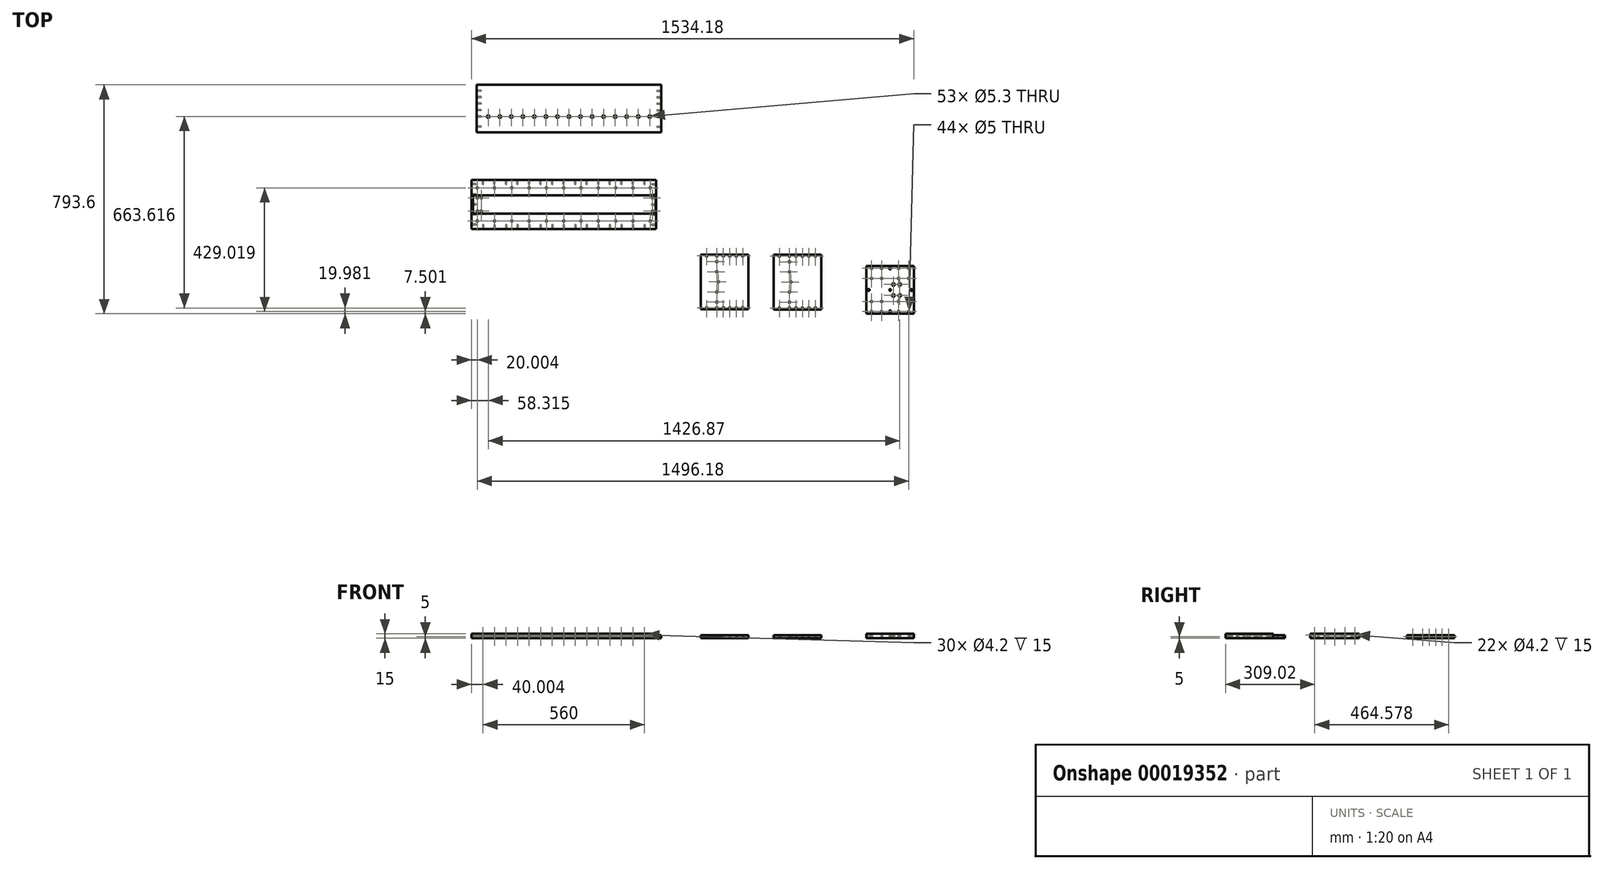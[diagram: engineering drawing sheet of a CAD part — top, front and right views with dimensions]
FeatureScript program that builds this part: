
annotation { "Feature Type Name" : "Feature", "Feature Type Description" : "" }
export const myFeature = defineFeature(function(context is Context, id is Id, definition is map)
    precondition{}
    {
        {
            var Q0;
            Q0=qCreatedBy(makeId("Top.planeOp"),FACE);
            var sketch = newSketch(context, id + "F0", { "sketchPlane" : qUnion([Q0])});
            skLineSegment(sketch, "E0.bottom", {"start": v(-320.38, 53) * mm, "end": v(319.62, 53) * mm});
            skLineSegment(sketch, "E0.top", {"start": v(-320.38, -117) * mm, "end": v(319.62, -117) * mm});
            skLineSegment(sketch, "E0.left", {"start": v(-320.38, 53) * mm, "end": v(-320.38, -117) * mm});
            skLineSegment(sketch, "E0.right", {"start": v(319.62, 53) * mm, "end": v(319.62, -117) * mm});
            skLineSegment(sketch, "E1.right", {"start": v(337.93, 382.58) * mm, "end": v(337.93, 217.58) * mm});
            skLineSegment(sketch, "E1.left", {"start": v(-302.07, 382.58) * mm, "end": v(-302.07, 217.58) * mm});
            skLineSegment(sketch, "E1.top", {"start": v(-302.07, 217.58) * mm, "end": v(337.93, 217.58) * mm});
            skLineSegment(sketch, "E1.bottom", {"start": v(-302.07, 382.58) * mm, "end": v(337.93, 382.58) * mm});
            skLineSegment(sketch, "E2.bottom", {"start": v(475.41, -205.5) * mm, "end": v(640.41, -205.5) * mm});
            skLineSegment(sketch, "E2.top", {"start": v(475.41, -395.5) * mm, "end": v(640.41, -395.5) * mm});
            skLineSegment(sketch, "E2.left", {"start": v(475.41, -205.5) * mm, "end": v(475.41, -395.5) * mm});
            skLineSegment(sketch, "E2.right", {"start": v(640.41, -205.5) * mm, "end": v(640.41, -395.5) * mm});
            skCircle(sketch, "E3", {"center": v(575.41, -210.5) * mm, "radius": 2.65 * mm});
            skCircle(sketch, "E4", {"center": v(620.41, -210.5) * mm, "radius": 2.65 * mm});
            skCircle(sketch, "E5", {"center": v(597.91, -210.5) * mm, "radius": 2.65 * mm});
            skCircle(sketch, "E6", {"center": v(552.91, -210.5) * mm, "radius": 2.65 * mm});
            skCircle(sketch, "E7", {"center": v(495.41, -210.5) * mm, "radius": 2.65 * mm});
            skCircle(sketch, "E8", {"center": v(530.41, -210.5) * mm, "radius": 2.65 * mm});
            skCircle(sketch, "E9", {"center": v(575.41, -390.5) * mm, "radius": 2.65 * mm});
            skCircle(sketch, "E10", {"center": v(552.91, -390.5) * mm, "radius": 2.65 * mm});
            skCircle(sketch, "E11", {"center": v(597.91, -390.5) * mm, "radius": 2.65 * mm});
            skCircle(sketch, "E12", {"center": v(620.41, -390.5) * mm, "radius": 2.65 * mm});
            skCircle(sketch, "E13", {"center": v(530.41, -390.5) * mm, "radius": 2.65 * mm});
            skCircle(sketch, "E14", {"center": v(495.41, -390.5) * mm, "radius": 2.65 * mm});
            skCircle(sketch, "E15", {"center": v(530.41, -230.5) * mm, "radius": 2.65 * mm});
            skCircle(sketch, "E16", {"center": v(530.41, -265.5) * mm, "radius": 2.65 * mm});
            skCircle(sketch, "E17", {"center": v(535.41, -300.5) * mm, "radius": 2.65 * mm});
            skCircle(sketch, "E18", {"center": v(530.41, -335.5) * mm, "radius": 2.65 * mm});
            skCircle(sketch, "E19", {"center": v(530.41, -370.5) * mm, "radius": 2.65 * mm});
            skLineSegment(sketch, "E20.top", {"start": v(727.45, -396.04) * mm, "end": v(892.45, -396.04) * mm});
            skLineSegment(sketch, "E20.bottom", {"start": v(727.45, -206.04) * mm, "end": v(892.45, -206.04) * mm});
            skLineSegment(sketch, "E20.right", {"start": v(892.45, -206.04) * mm, "end": v(892.45, -396.04) * mm});
            skLineSegment(sketch, "E20.left", {"start": v(727.45, -206.04) * mm, "end": v(727.45, -396.04) * mm});
            skCircle(sketch, "E21", {"center": v(849.95, -211.04) * mm, "radius": 2.65 * mm});
            skCircle(sketch, "E22", {"center": v(804.95, -391.04) * mm, "radius": 2.65 * mm});
            skCircle(sketch, "E23", {"center": v(787.45, -301.04) * mm, "radius": 2.65 * mm});
            skCircle(sketch, "E24", {"center": v(872.45, -211.04) * mm, "radius": 2.65 * mm});
            skCircle(sketch, "E25", {"center": v(782.45, -231.04) * mm, "radius": 2.65 * mm});
            skCircle(sketch, "E26", {"center": v(782.45, -266.04) * mm, "radius": 2.65 * mm});
            skCircle(sketch, "E27", {"center": v(849.95, -391.04) * mm, "radius": 2.65 * mm});
            skCircle(sketch, "E28", {"center": v(782.45, -211.04) * mm, "radius": 2.65 * mm});
            skCircle(sketch, "E29", {"center": v(872.45, -391.04) * mm, "radius": 2.65 * mm});
            skCircle(sketch, "E30", {"center": v(804.95, -211.04) * mm, "radius": 2.65 * mm});
            skCircle(sketch, "E31", {"center": v(782.45, -391.04) * mm, "radius": 2.65 * mm});
            skCircle(sketch, "E32", {"center": v(782.45, -336.04) * mm, "radius": 2.65 * mm});
            skCircle(sketch, "E33", {"center": v(747.45, -391.04) * mm, "radius": 2.65 * mm});
            skCircle(sketch, "E34", {"center": v(782.45, -371.04) * mm, "radius": 2.65 * mm});
            skCircle(sketch, "E35", {"center": v(747.45, -211.04) * mm, "radius": 2.65 * mm});
            skCircle(sketch, "E36", {"center": v(827.45, -391.04) * mm, "radius": 2.65 * mm});
            skCircle(sketch, "E37", {"center": v(827.45, -211.04) * mm, "radius": 2.65 * mm});
            skCircle(sketch, "E38", {"center": v(-300.38, -89.5) * mm, "radius": 2.5 * mm});
            skCircle(sketch, "E39", {"center": v(-240.38, -89.5) * mm, "radius": 2.5 * mm});
            skCircle(sketch, "E40", {"center": v(-180.38, -89.5) * mm, "radius": 2.5 * mm});
            skCircle(sketch, "E41", {"center": v(-120.38, -89.5) * mm, "radius": 2.5 * mm});
            skCircle(sketch, "E42", {"center": v(-60.38, -89.5) * mm, "radius": 2.5 * mm});
            skCircle(sketch, "E43", {"center": v(-0.38, -89.5) * mm, "radius": 2.5 * mm});
            skCircle(sketch, "E44", {"center": v(59.62, -89.5) * mm, "radius": 2.5 * mm});
            skCircle(sketch, "E45", {"center": v(119.62, -89.5) * mm, "radius": 2.5 * mm});
            skCircle(sketch, "E46", {"center": v(179.62, -89.5) * mm, "radius": 2.5 * mm});
            skCircle(sketch, "E47", {"center": v(239.62, -89.5) * mm, "radius": 2.5 * mm});
            skCircle(sketch, "E48", {"center": v(299.62, -89.5) * mm, "radius": 2.5 * mm});
            skCircle(sketch, "E49", {"center": v(-180.38, 25.5) * mm, "radius": 2.5 * mm});
            skCircle(sketch, "E50", {"center": v(-120.38, 25.5) * mm, "radius": 2.5 * mm});
            skCircle(sketch, "E51", {"center": v(119.62, 25.5) * mm, "radius": 2.5 * mm});
            skCircle(sketch, "E52", {"center": v(-60.38, 25.5) * mm, "radius": 2.5 * mm});
            skCircle(sketch, "E53", {"center": v(-0.38, 25.5) * mm, "radius": 2.5 * mm});
            skCircle(sketch, "E54", {"center": v(239.62, 25.5) * mm, "radius": 2.5 * mm});
            skCircle(sketch, "E55", {"center": v(-240.38, 25.5) * mm, "radius": 2.5 * mm});
            skCircle(sketch, "E56", {"center": v(299.62, 25.5) * mm, "radius": 2.5 * mm});
            skCircle(sketch, "E57", {"center": v(59.62, 25.5) * mm, "radius": 2.5 * mm});
            skCircle(sketch, "E58", {"center": v(179.62, 25.5) * mm, "radius": 2.5 * mm});
            skCircle(sketch, "E59", {"center": v(-300.38, 25.5) * mm, "radius": 2.5 * mm});
            skCircle(sketch, "E60", {"center": v(307.62, -9) * mm, "radius": 2.5 * mm});
            skCircle(sketch, "E61", {"center": v(307.62, -55) * mm, "radius": 2.5 * mm});
            skPoint(sketch, "E62", {"position": v(319.62, -32) * mm});
            skCircle(sketch, "E63", {"center": v(-299.38, -9) * mm, "radius": 2.5 * mm});
            skCircle(sketch, "E64", {"center": v(-299.38, -55) * mm, "radius": 2.5 * mm});
            skCircle(sketch, "E65", {"center": v(-286.38, -9) * mm, "radius": 2.5 * mm});
            skCircle(sketch, "E66", {"center": v(-286.38, -55) * mm, "radius": 2.5 * mm});
            skPoint(sketch, "E67", {"position": v(-320.38, -32) * mm});
            skLineSegment(sketch, "E68.bottom", {"start": v(1048.8, -246.02) * mm, "end": v(1213.8, -246.02) * mm});
            skLineSegment(sketch, "E68.top", {"start": v(1048.8, -411.02) * mm, "end": v(1213.8, -411.02) * mm});
            skLineSegment(sketch, "E68.left", {"start": v(1048.8, -246.02) * mm, "end": v(1048.8, -411.02) * mm});
            skLineSegment(sketch, "E68.right", {"start": v(1213.8, -246.02) * mm, "end": v(1213.8, -411.02) * mm});
            skCircle(sketch, "E69", {"center": v(1066.8, -253.52) * mm, "radius": 2.5 * mm});
            skCircle(sketch, "E70", {"center": v(1101.8, -253.52) * mm, "radius": 2.5 * mm});
            skCircle(sketch, "E71", {"center": v(1066.8, -288.52) * mm, "radius": 2.5 * mm});
            skCircle(sketch, "E72", {"center": v(1101.8, -288.52) * mm, "radius": 2.5 * mm});
            skCircle(sketch, "E73", {"center": v(1160.8, -253.52) * mm, "radius": 2.5 * mm});
            skCircle(sketch, "E74", {"center": v(1195.8, -288.52) * mm, "radius": 2.5 * mm});
            skCircle(sketch, "E75", {"center": v(1160.8, -288.52) * mm, "radius": 2.5 * mm});
            skCircle(sketch, "E76", {"center": v(1195.8, -253.52) * mm, "radius": 2.5 * mm});
            skCircle(sketch, "E77", {"center": v(1066.8, -368.52) * mm, "radius": 2.5 * mm});
            skCircle(sketch, "E78", {"center": v(1101.8, -403.52) * mm, "radius": 2.5 * mm});
            skCircle(sketch, "E79", {"center": v(1066.8, -403.52) * mm, "radius": 2.5 * mm});
            skCircle(sketch, "E80", {"center": v(1101.8, -368.52) * mm, "radius": 2.5 * mm});
            skCircle(sketch, "E81", {"center": v(1160.8, -368.52) * mm, "radius": 2.5 * mm});
            skCircle(sketch, "E82", {"center": v(1195.8, -403.52) * mm, "radius": 2.5 * mm});
            skCircle(sketch, "E83", {"center": v(1160.8, -403.52) * mm, "radius": 2.5 * mm});
            skCircle(sketch, "E84", {"center": v(1195.8, -368.52) * mm, "radius": 2.5 * mm});
            skPoint(sketch, "E85", {"position": v(1048.8, -328.52) * mm});
            skPoint(sketch, "E86", {"position": v(1131.3, -411.02) * mm});
            skCircle(sketch, "E87", {"center": v(1056.8, -328.52) * mm, "radius": 3.35 * mm});
            skCircle(sketch, "E88", {"center": v(1205.8, -328.52) * mm, "radius": 3.35 * mm});
            skCircle(sketch, "E89", {"center": v(1131.3, -403.02) * mm, "radius": 3.35 * mm});
            skCircle(sketch, "E90", {"center": v(1131.3, -254.02) * mm, "radius": 3.35 * mm});
            skCircle(sketch, "E91", {"center": v(1131.3, -328.52) * mm, "radius": 3 * mm});
            skCircle(sketch, "E92", {"center": v(1142.8, -309.52) * mm, "radius": 2.65 * mm});
            skCircle(sketch, "E93", {"center": v(1164.8, -309.52) * mm, "radius": 2.65 * mm});
            skCircle(sketch, "E94", {"center": v(1142.8, -347.52) * mm, "radius": 2.65 * mm});
            skCircle(sketch, "E95", {"center": v(1164.8, -347.52) * mm, "radius": 2.65 * mm});
            skCircle(sketch, "E96", {"center": v(1142.8, -309.52) * mm, "radius": 4.75 * mm});
            skCircle(sketch, "E97", {"center": v(1164.8, -309.52) * mm, "radius": 4.75 * mm});
            skCircle(sketch, "E98", {"center": v(1142.8, -347.52) * mm, "radius": 4.75 * mm});
            skCircle(sketch, "E99", {"center": v(1164.8, -347.52) * mm, "radius": 4.75 * mm});
            skSolve(sketch);
        }
        {
            var Q0;
            Q0=makeQuery(id+"F0.imprint","IMPRINT",FACE,{"disambiguationData":[TD([[makeQuery(id+"F0.imprint","IMPRINT",EDGE,{"derivedFrom":sQuery(id+"F0.wireOp",EDGE,"E0.bottom")}),-1.0]])]});
            var Q1;
            Q1=makeQuery(id+"F0.imprint","IMPRINT",FACE,{"disambiguationData":[TD([[makeQuery(id+"F0.imprint","IMPRINT",EDGE,{"derivedFrom":sQuery(id+"F0.wireOp",EDGE,"E60")}),-1.0]])]});
            extrude(context, id + "F1", {"entities" : qUnion([Q0, Q1]), "depth" : 15 * mm});
        }
        {
            var Q0;
            Q0=makeQuery(id+"F0.imprint","IMPRINT",FACE,{"disambiguationData":[TD([[makeQuery(id+"F0.imprint","IMPRINT",EDGE,{"derivedFrom":sQuery(id+"F0.wireOp",EDGE,"E1.right")}),-1.0]])]});
            extrude(context, id + "F2", {"entities" : qUnion([Q0]), "depth" : 10 * mm});
        }
        {
            var Q0;
            Q0=makeQuery(id+"F1.opExtrude","SWEPT_FACE",FACE,{"disambiguationData":[OSD([sQuery(id+"F0.wireOp",EDGE,"E0.top")])]});
            var sketch = newSketch(context, id + "F3", { "sketchPlane" : qUnion([Q0])});
            skCircle(sketch, "E100", {"center": v(-0.38, 10) * mm, "radius": 2.1 * mm});
            skCircle(sketch, "E101", {"center": v(39.62, 10) * mm, "radius": 2.1 * mm});
            skCircle(sketch, "E102", {"center": v(79.62, 10) * mm, "radius": 2.1 * mm});
            skCircle(sketch, "E103", {"center": v(119.62, 10) * mm, "radius": 2.1 * mm});
            skCircle(sketch, "E104", {"center": v(159.62, 10) * mm, "radius": 2.1 * mm});
            skCircle(sketch, "E105", {"center": v(199.62, 10) * mm, "radius": 2.1 * mm});
            skCircle(sketch, "E106", {"center": v(239.62, 10) * mm, "radius": 2.1 * mm});
            skCircle(sketch, "E107", {"center": v(-40.38, 10) * mm, "radius": 2.1 * mm});
            skCircle(sketch, "E108", {"center": v(-80.38, 10) * mm, "radius": 2.1 * mm});
            skCircle(sketch, "E109", {"center": v(-120.38, 10) * mm, "radius": 2.1 * mm});
            skCircle(sketch, "E110", {"center": v(-160.38, 10) * mm, "radius": 2.1 * mm});
            skCircle(sketch, "E111", {"center": v(-200.38, 10) * mm, "radius": 2.1 * mm});
            skCircle(sketch, "E112", {"center": v(-240.38, 10) * mm, "radius": 2.1 * mm});
            skCircle(sketch, "E113", {"center": v(279.62, 10) * mm, "radius": 2.1 * mm});
            skCircle(sketch, "E114", {"center": v(-280.38, 10) * mm, "radius": 2.1 * mm});
            skSolve(sketch);
        }
        {
            var Q0;
            Q0=makeQuery(id+"F1.opExtrude","SWEPT_FACE",FACE,{"disambiguationData":[OSD([sQuery(id+"F0.wireOp",EDGE,"E0.bottom")])]});
            var sketch = newSketch(context, id + "F4", { "sketchPlane" : qUnion([Q0])});
            skCircle(sketch, "E115", {"center": v(120.38, 5) * mm, "radius": 2.1 * mm});
            skCircle(sketch, "E116", {"center": v(280.38, 5) * mm, "radius": 2.1 * mm});
            skCircle(sketch, "E117", {"center": v(0.38, 5) * mm, "radius": 2.1 * mm});
            skCircle(sketch, "E118", {"center": v(-239.62, 5) * mm, "radius": 2.1 * mm});
            skCircle(sketch, "E119", {"center": v(-199.62, 5) * mm, "radius": 2.1 * mm});
            skCircle(sketch, "E120", {"center": v(-159.62, 5) * mm, "radius": 2.1 * mm});
            skCircle(sketch, "E121", {"center": v(-119.62, 5) * mm, "radius": 2.1 * mm});
            skCircle(sketch, "E122", {"center": v(-79.62, 5) * mm, "radius": 2.1 * mm});
            skCircle(sketch, "E123", {"center": v(-39.62, 5) * mm, "radius": 2.1 * mm});
            skCircle(sketch, "E124", {"center": v(80.38, 5) * mm, "radius": 2.1 * mm});
            skCircle(sketch, "E125", {"center": v(240.38, 5) * mm, "radius": 2.1 * mm});
            skCircle(sketch, "E126", {"center": v(-279.62, 5) * mm, "radius": 2.1 * mm});
            skCircle(sketch, "E127", {"center": v(200.38, 5) * mm, "radius": 2.1 * mm});
            skCircle(sketch, "E128", {"center": v(160.38, 5) * mm, "radius": 2.1 * mm});
            skCircle(sketch, "E129", {"center": v(40.38, 5) * mm, "radius": 2.1 * mm});
            skSolve(sketch);
        }
        {
            var Q0;
            Q0=makeQuery(id+"F4.imprint","IMPRINT",FACE,{"disambiguationData":[TD([[makeQuery(id+"F4.imprint","IMPRINT",EDGE,{"derivedFrom":sQuery(id+"F4.wireOp",EDGE,"E116")}),1.0]])]});
            var Q1;
            Q1=makeQuery(id+"F4.imprint","IMPRINT",FACE,{"disambiguationData":[TD([[makeQuery(id+"F4.imprint","IMPRINT",EDGE,{"derivedFrom":sQuery(id+"F4.wireOp",EDGE,"E125")}),1.0]])]});
            var Q2;
            Q2=makeQuery(id+"F4.imprint","IMPRINT",FACE,{"disambiguationData":[TD([[makeQuery(id+"F4.imprint","IMPRINT",EDGE,{"derivedFrom":sQuery(id+"F4.wireOp",EDGE,"E127")}),1.0]])]});
            var Q3;
            Q3=makeQuery(id+"F4.imprint","IMPRINT",FACE,{"disambiguationData":[TD([[makeQuery(id+"F4.imprint","IMPRINT",EDGE,{"derivedFrom":sQuery(id+"F4.wireOp",EDGE,"E128")}),1.0]])]});
            var Q4;
            Q4=makeQuery(id+"F4.imprint","IMPRINT",FACE,{"disambiguationData":[TD([[makeQuery(id+"F4.imprint","IMPRINT",EDGE,{"derivedFrom":sQuery(id+"F4.wireOp",EDGE,"E115")}),1.0]])]});
            var Q5;
            Q5=makeQuery(id+"F4.imprint","IMPRINT",FACE,{"disambiguationData":[TD([[makeQuery(id+"F4.imprint","IMPRINT",EDGE,{"derivedFrom":sQuery(id+"F4.wireOp",EDGE,"E124")}),1.0]])]});
            var Q6;
            Q6=makeQuery(id+"F4.imprint","IMPRINT",FACE,{"disambiguationData":[TD([[makeQuery(id+"F4.imprint","IMPRINT",EDGE,{"derivedFrom":sQuery(id+"F4.wireOp",EDGE,"E129")}),1.0]])]});
            var Q7;
            Q7=makeQuery(id+"F4.imprint","IMPRINT",FACE,{"disambiguationData":[TD([[makeQuery(id+"F4.imprint","IMPRINT",EDGE,{"derivedFrom":sQuery(id+"F4.wireOp",EDGE,"E117")}),1.0]])]});
            var Q8;
            Q8=makeQuery(id+"F4.imprint","IMPRINT",FACE,{"disambiguationData":[TD([[makeQuery(id+"F4.imprint","IMPRINT",EDGE,{"derivedFrom":sQuery(id+"F4.wireOp",EDGE,"E123")}),1.0]])]});
            var Q9;
            Q9=makeQuery(id+"F4.imprint","IMPRINT",FACE,{"disambiguationData":[TD([[makeQuery(id+"F4.imprint","IMPRINT",EDGE,{"derivedFrom":sQuery(id+"F4.wireOp",EDGE,"E122")}),1.0]])]});
            var Q10;
            Q10=makeQuery(id+"F4.imprint","IMPRINT",FACE,{"disambiguationData":[TD([[makeQuery(id+"F4.imprint","IMPRINT",EDGE,{"derivedFrom":sQuery(id+"F4.wireOp",EDGE,"E121")}),1.0]])]});
            var Q11;
            Q11=makeQuery(id+"F4.imprint","IMPRINT",FACE,{"disambiguationData":[TD([[makeQuery(id+"F4.imprint","IMPRINT",EDGE,{"derivedFrom":sQuery(id+"F4.wireOp",EDGE,"E120")}),1.0]])]});
            var Q12;
            Q12=makeQuery(id+"F4.imprint","IMPRINT",FACE,{"disambiguationData":[TD([[makeQuery(id+"F4.imprint","IMPRINT",EDGE,{"derivedFrom":sQuery(id+"F4.wireOp",EDGE,"E119")}),1.0]])]});
            var Q13;
            Q13=makeQuery(id+"F4.imprint","IMPRINT",FACE,{"disambiguationData":[TD([[makeQuery(id+"F4.imprint","IMPRINT",EDGE,{"derivedFrom":sQuery(id+"F4.wireOp",EDGE,"E118")}),1.0]])]});
            var Q14;
            Q14=makeQuery(id+"F4.imprint","IMPRINT",FACE,{"disambiguationData":[TD([[makeQuery(id+"F4.imprint","IMPRINT",EDGE,{"derivedFrom":sQuery(id+"F4.wireOp",EDGE,"E126")}),1.0]])]});
            extrude(context, id + "F5", {"entities" : qUnion([Q0, Q1, Q2, Q3, Q4, Q5, Q6, Q7, Q8, Q9, Q10, Q11, Q12, Q13, Q14]), "operationType" : NewBodyOperationType.REMOVE, "oppositeDirection" : true, "depth" : 15 * mm});
        }
        {
            var Q0;
            Q0=makeQuery(id+"F3.imprint","IMPRINT",FACE,{"disambiguationData":[TD([[makeQuery(id+"F3.imprint","IMPRINT",EDGE,{"derivedFrom":sQuery(id+"F3.wireOp",EDGE,"E113")}),1.0]])]});
            var Q1;
            Q1=makeQuery(id+"F3.imprint","IMPRINT",FACE,{"disambiguationData":[TD([[makeQuery(id+"F3.imprint","IMPRINT",EDGE,{"derivedFrom":sQuery(id+"F3.wireOp",EDGE,"E106")}),1.0]])]});
            var Q2;
            Q2=makeQuery(id+"F3.imprint","IMPRINT",FACE,{"disambiguationData":[TD([[makeQuery(id+"F3.imprint","IMPRINT",EDGE,{"derivedFrom":sQuery(id+"F3.wireOp",EDGE,"E105")}),1.0]])]});
            var Q3;
            Q3=makeQuery(id+"F3.imprint","IMPRINT",FACE,{"disambiguationData":[TD([[makeQuery(id+"F3.imprint","IMPRINT",EDGE,{"derivedFrom":sQuery(id+"F3.wireOp",EDGE,"E104")}),1.0]])]});
            var Q4;
            Q4=makeQuery(id+"F3.imprint","IMPRINT",FACE,{"disambiguationData":[TD([[makeQuery(id+"F3.imprint","IMPRINT",EDGE,{"derivedFrom":sQuery(id+"F3.wireOp",EDGE,"E103")}),1.0]])]});
            var Q5;
            Q5=makeQuery(id+"F3.imprint","IMPRINT",FACE,{"disambiguationData":[TD([[makeQuery(id+"F3.imprint","IMPRINT",EDGE,{"derivedFrom":sQuery(id+"F3.wireOp",EDGE,"E102")}),1.0]])]});
            var Q6;
            Q6=makeQuery(id+"F3.imprint","IMPRINT",FACE,{"disambiguationData":[TD([[makeQuery(id+"F3.imprint","IMPRINT",EDGE,{"derivedFrom":sQuery(id+"F3.wireOp",EDGE,"E101")}),1.0]])]});
            var Q7;
            Q7=makeQuery(id+"F3.imprint","IMPRINT",FACE,{"disambiguationData":[TD([[makeQuery(id+"F3.imprint","IMPRINT",EDGE,{"derivedFrom":sQuery(id+"F3.wireOp",EDGE,"E100")}),1.0]])]});
            var Q8;
            Q8=makeQuery(id+"F3.imprint","IMPRINT",FACE,{"disambiguationData":[TD([[makeQuery(id+"F3.imprint","IMPRINT",EDGE,{"derivedFrom":sQuery(id+"F3.wireOp",EDGE,"E107")}),1.0]])]});
            var Q9;
            Q9=makeQuery(id+"F3.imprint","IMPRINT",FACE,{"disambiguationData":[TD([[makeQuery(id+"F3.imprint","IMPRINT",EDGE,{"derivedFrom":sQuery(id+"F3.wireOp",EDGE,"E108")}),1.0]])]});
            var Q10;
            Q10=makeQuery(id+"F3.imprint","IMPRINT",FACE,{"disambiguationData":[TD([[makeQuery(id+"F3.imprint","IMPRINT",EDGE,{"derivedFrom":sQuery(id+"F3.wireOp",EDGE,"E109")}),1.0]])]});
            var Q11;
            Q11=makeQuery(id+"F3.imprint","IMPRINT",FACE,{"disambiguationData":[TD([[makeQuery(id+"F3.imprint","IMPRINT",EDGE,{"derivedFrom":sQuery(id+"F3.wireOp",EDGE,"E110")}),1.0]])]});
            var Q12;
            Q12=makeQuery(id+"F3.imprint","IMPRINT",FACE,{"disambiguationData":[TD([[makeQuery(id+"F3.imprint","IMPRINT",EDGE,{"derivedFrom":sQuery(id+"F3.wireOp",EDGE,"E111")}),1.0]])]});
            var Q13;
            Q13=makeQuery(id+"F3.imprint","IMPRINT",FACE,{"disambiguationData":[TD([[makeQuery(id+"F3.imprint","IMPRINT",EDGE,{"derivedFrom":sQuery(id+"F3.wireOp",EDGE,"E112")}),1.0]])]});
            var Q14;
            Q14=makeQuery(id+"F3.imprint","IMPRINT",FACE,{"disambiguationData":[TD([[makeQuery(id+"F3.imprint","IMPRINT",EDGE,{"derivedFrom":sQuery(id+"F3.wireOp",EDGE,"E114")}),1.0]])]});
            extrude(context, id + "F6", {"entities" : qUnion([Q0, Q1, Q2, Q3, Q4, Q5, Q6, Q7, Q8, Q9, Q10, Q11, Q12, Q13, Q14]), "operationType" : NewBodyOperationType.REMOVE, "oppositeDirection" : true, "depth" : 15 * mm});
        }
        {
            var Q0;
            Q0=makeQuery(id+"F1.opExtrude","SWEPT_FACE",FACE,{"disambiguationData":[OSD([sQuery(id+"F0.wireOp",EDGE,"E0.left")])]});
            var sketch = newSketch(context, id + "F7", { "sketchPlane" : qUnion([Q0])});
            skCircle(sketch, "E130", {"center": v(-38, 10) * mm, "radius": 2.1 * mm});
            skCircle(sketch, "E131", {"center": v(-3, 10) * mm, "radius": 2.1 * mm});
            skCircle(sketch, "E132", {"center": v(32, 5) * mm, "radius": 2.1 * mm});
            skCircle(sketch, "E133", {"center": v(67, 10) * mm, "radius": 2.1 * mm});
            skCircle(sketch, "E134", {"center": v(102, 10) * mm, "radius": 2.1 * mm});
            skSolve(sketch);
        }
        {
            var Q0;
            Q0=makeQuery(id+"F7.imprint","IMPRINT",FACE,{"disambiguationData":[TD([[makeQuery(id+"F7.imprint","IMPRINT",EDGE,{"derivedFrom":sQuery(id+"F7.wireOp",EDGE,"E130")}),1.0]])]});
            var Q1;
            Q1=makeQuery(id+"F7.imprint","IMPRINT",FACE,{"disambiguationData":[TD([[makeQuery(id+"F7.imprint","IMPRINT",EDGE,{"derivedFrom":sQuery(id+"F7.wireOp",EDGE,"E131")}),1.0]])]});
            var Q2;
            Q2=makeQuery(id+"F7.imprint","IMPRINT",FACE,{"disambiguationData":[TD([[makeQuery(id+"F7.imprint","IMPRINT",EDGE,{"derivedFrom":sQuery(id+"F7.wireOp",EDGE,"E132")}),1.0]])]});
            var Q3;
            Q3=makeQuery(id+"F7.imprint","IMPRINT",FACE,{"disambiguationData":[TD([[makeQuery(id+"F7.imprint","IMPRINT",EDGE,{"derivedFrom":sQuery(id+"F7.wireOp",EDGE,"E133")}),1.0]])]});
            var Q4;
            Q4=makeQuery(id+"F7.imprint","IMPRINT",FACE,{"disambiguationData":[TD([[makeQuery(id+"F7.imprint","IMPRINT",EDGE,{"derivedFrom":sQuery(id+"F7.wireOp",EDGE,"E134")}),1.0]])]});
            extrude(context, id + "F8", {"entities" : qUnion([Q0, Q1, Q2, Q3, Q4]), "operationType" : NewBodyOperationType.REMOVE, "oppositeDirection" : true, "depth" : 15 * mm});
        }
        {
            var Q0;
            Q0=makeQuery(id+"F1.opExtrude","SWEPT_FACE",FACE,{"disambiguationData":[OSD([sQuery(id+"F0.wireOp",EDGE,"E0.right")])]});
            var sketch = newSketch(context, id + "F9", { "sketchPlane" : qUnion([Q0])});
            skCircle(sketch, "E135", {"center": v(-102, 10) * mm, "radius": 2.1 * mm});
            skCircle(sketch, "E136", {"center": v(-67, 10) * mm, "radius": 2.1 * mm});
            skCircle(sketch, "E137", {"center": v(38, 10) * mm, "radius": 2.1 * mm});
            skCircle(sketch, "E138", {"center": v(3, 10) * mm, "radius": 2.1 * mm});
            skCircle(sketch, "E139", {"center": v(-32, 5) * mm, "radius": 2.1 * mm});
            skSolve(sketch);
        }
        {
            var Q0;
            Q0=makeQuery(id+"F9.imprint","IMPRINT",FACE,{"disambiguationData":[TD([[makeQuery(id+"F9.imprint","IMPRINT",EDGE,{"derivedFrom":sQuery(id+"F9.wireOp",EDGE,"E135")}),1.0]])]});
            var Q1;
            Q1=makeQuery(id+"F9.imprint","IMPRINT",FACE,{"disambiguationData":[TD([[makeQuery(id+"F9.imprint","IMPRINT",EDGE,{"derivedFrom":sQuery(id+"F9.wireOp",EDGE,"E136")}),1.0]])]});
            var Q2;
            Q2=makeQuery(id+"F9.imprint","IMPRINT",FACE,{"disambiguationData":[TD([[makeQuery(id+"F9.imprint","IMPRINT",EDGE,{"derivedFrom":sQuery(id+"F9.wireOp",EDGE,"E139")}),1.0]])]});
            var Q3;
            Q3=makeQuery(id+"F9.imprint","IMPRINT",FACE,{"disambiguationData":[TD([[makeQuery(id+"F9.imprint","IMPRINT",EDGE,{"derivedFrom":sQuery(id+"F9.wireOp",EDGE,"E138")}),1.0]])]});
            var Q4;
            Q4=makeQuery(id+"F9.imprint","IMPRINT",FACE,{"disambiguationData":[TD([[makeQuery(id+"F9.imprint","IMPRINT",EDGE,{"derivedFrom":sQuery(id+"F9.wireOp",EDGE,"E137")}),1.0]])]});
            extrude(context, id + "F10", {"entities" : qUnion([Q0, Q1, Q2, Q3, Q4]), "operationType" : NewBodyOperationType.REMOVE, "oppositeDirection" : true, "depth" : 15 * mm});
        }
        {
            var Q0;
            Q0=makeQuery(id+"F2.opExtrude","CAP_FACE",FACE,{"disambiguationData":[OSD([sQuery(id+"F0.wireOp",EDGE,"E1.right"),sQuery(id+"F0.wireOp",EDGE,"E1.left"),sQuery(id+"F0.wireOp",EDGE,"E1.top"),sQuery(id+"F0.wireOp",EDGE,"E1.bottom")])],"isStart":false});
            var sketch = newSketch(context, id + "F11", { "sketchPlane" : qUnion([Q0])});
            skCircle(sketch, "E140", {"center": v(257.93, 272.58) * mm, "radius": 2.65 * mm});
            skCircle(sketch, "E141", {"center": v(217.93, 272.58) * mm, "radius": 2.65 * mm});
            skCircle(sketch, "E142", {"center": v(177.93, 272.58) * mm, "radius": 2.65 * mm});
            skCircle(sketch, "E143", {"center": v(137.93, 272.58) * mm, "radius": 2.65 * mm});
            skCircle(sketch, "E144", {"center": v(97.93, 272.58) * mm, "radius": 2.65 * mm});
            skCircle(sketch, "E145", {"center": v(57.93, 272.58) * mm, "radius": 2.65 * mm});
            skCircle(sketch, "E146", {"center": v(17.93, 272.58) * mm, "radius": 2.65 * mm});
            skCircle(sketch, "E147", {"center": v(-262.07, 272.58) * mm, "radius": 2.65 * mm});
            skCircle(sketch, "E148", {"center": v(-142.07, 272.58) * mm, "radius": 2.65 * mm});
            skCircle(sketch, "E149", {"center": v(-102.07, 272.58) * mm, "radius": 2.65 * mm});
            skCircle(sketch, "E150", {"center": v(297.93, 272.58) * mm, "radius": 2.65 * mm});
            skCircle(sketch, "E151", {"center": v(-62.07, 272.58) * mm, "radius": 2.65 * mm});
            skCircle(sketch, "E152", {"center": v(-222.07, 272.58) * mm, "radius": 2.65 * mm});
            skCircle(sketch, "E153", {"center": v(-182.07, 272.58) * mm, "radius": 2.65 * mm});
            skCircle(sketch, "E154", {"center": v(-22.07, 272.58) * mm, "radius": 2.65 * mm});
            skCircle(sketch, "E155", {"center": v(-262.07, 272.58) * mm, "radius": 4.75 * mm});
            skCircle(sketch, "E156", {"center": v(-222.07, 272.58) * mm, "radius": 4.75 * mm});
            skCircle(sketch, "E157", {"center": v(-182.07, 272.58) * mm, "radius": 4.75 * mm});
            skCircle(sketch, "E158", {"center": v(-142.07, 272.58) * mm, "radius": 4.75 * mm});
            skCircle(sketch, "E159", {"center": v(-102.07, 272.58) * mm, "radius": 4.75 * mm});
            skCircle(sketch, "E160", {"center": v(-62.07, 272.58) * mm, "radius": 4.75 * mm});
            skCircle(sketch, "E161", {"center": v(-22.07, 272.58) * mm, "radius": 4.75 * mm});
            skCircle(sketch, "E162", {"center": v(17.93, 272.58) * mm, "radius": 4.75 * mm});
            skCircle(sketch, "E163", {"center": v(57.93, 272.58) * mm, "radius": 4.75 * mm});
            skCircle(sketch, "E164", {"center": v(97.93, 272.58) * mm, "radius": 4.75 * mm});
            skCircle(sketch, "E165", {"center": v(137.93, 272.58) * mm, "radius": 4.75 * mm});
            skCircle(sketch, "E166", {"center": v(177.93, 272.58) * mm, "radius": 4.75 * mm});
            skCircle(sketch, "E167", {"center": v(217.93, 272.58) * mm, "radius": 4.75 * mm});
            skCircle(sketch, "E168", {"center": v(257.93, 272.58) * mm, "radius": 4.75 * mm});
            skCircle(sketch, "E169", {"center": v(297.93, 272.58) * mm, "radius": 4.75 * mm});
            skSolve(sketch);
        }
        {
            var Q0;
            Q0=makeQuery(id+"F11.imprint","IMPRINT",FACE,{"disambiguationData":[TD([[makeQuery(id+"F11.imprint","IMPRINT",EDGE,{"derivedFrom":sQuery(id+"F11.wireOp",EDGE,"E147")}),1.0]])]});
            var Q1;
            Q1=makeQuery(id+"F11.imprint","IMPRINT",FACE,{"disambiguationData":[TD([[makeQuery(id+"F11.imprint","IMPRINT",EDGE,{"derivedFrom":sQuery(id+"F11.wireOp",EDGE,"E152")}),1.0]])]});
            var Q2;
            Q2=makeQuery(id+"F11.imprint","IMPRINT",FACE,{"disambiguationData":[TD([[makeQuery(id+"F11.imprint","IMPRINT",EDGE,{"derivedFrom":sQuery(id+"F11.wireOp",EDGE,"E153")}),1.0]])]});
            var Q3;
            Q3=makeQuery(id+"F11.imprint","IMPRINT",FACE,{"disambiguationData":[TD([[makeQuery(id+"F11.imprint","IMPRINT",EDGE,{"derivedFrom":sQuery(id+"F11.wireOp",EDGE,"E148")}),1.0]])]});
            var Q4;
            Q4=makeQuery(id+"F11.imprint","IMPRINT",FACE,{"disambiguationData":[TD([[makeQuery(id+"F11.imprint","IMPRINT",EDGE,{"derivedFrom":sQuery(id+"F11.wireOp",EDGE,"E149")}),1.0]])]});
            var Q5;
            Q5=makeQuery(id+"F11.imprint","IMPRINT",FACE,{"disambiguationData":[TD([[makeQuery(id+"F11.imprint","IMPRINT",EDGE,{"derivedFrom":sQuery(id+"F11.wireOp",EDGE,"E151")}),1.0]])]});
            var Q6;
            Q6=makeQuery(id+"F11.imprint","IMPRINT",FACE,{"disambiguationData":[TD([[makeQuery(id+"F11.imprint","IMPRINT",EDGE,{"derivedFrom":sQuery(id+"F11.wireOp",EDGE,"E154")}),1.0]])]});
            var Q7;
            Q7=makeQuery(id+"F11.imprint","IMPRINT",FACE,{"disambiguationData":[TD([[makeQuery(id+"F11.imprint","IMPRINT",EDGE,{"derivedFrom":sQuery(id+"F11.wireOp",EDGE,"E146")}),1.0]])]});
            var Q8;
            Q8=makeQuery(id+"F11.imprint","IMPRINT",FACE,{"disambiguationData":[TD([[makeQuery(id+"F11.imprint","IMPRINT",EDGE,{"derivedFrom":sQuery(id+"F11.wireOp",EDGE,"E145")}),1.0]])]});
            var Q9;
            Q9=makeQuery(id+"F11.imprint","IMPRINT",FACE,{"disambiguationData":[TD([[makeQuery(id+"F11.imprint","IMPRINT",EDGE,{"derivedFrom":sQuery(id+"F11.wireOp",EDGE,"E144")}),1.0]])]});
            var Q10;
            Q10=makeQuery(id+"F11.imprint","IMPRINT",FACE,{"disambiguationData":[TD([[makeQuery(id+"F11.imprint","IMPRINT",EDGE,{"derivedFrom":sQuery(id+"F11.wireOp",EDGE,"E143")}),1.0]])]});
            var Q11;
            Q11=makeQuery(id+"F11.imprint","IMPRINT",FACE,{"disambiguationData":[TD([[makeQuery(id+"F11.imprint","IMPRINT",EDGE,{"derivedFrom":sQuery(id+"F11.wireOp",EDGE,"E142")}),1.0]])]});
            var Q12;
            Q12=makeQuery(id+"F11.imprint","IMPRINT",FACE,{"disambiguationData":[TD([[makeQuery(id+"F11.imprint","IMPRINT",EDGE,{"derivedFrom":sQuery(id+"F11.wireOp",EDGE,"E141")}),1.0]])]});
            var Q13;
            Q13=makeQuery(id+"F11.imprint","IMPRINT",FACE,{"disambiguationData":[TD([[makeQuery(id+"F11.imprint","IMPRINT",EDGE,{"derivedFrom":sQuery(id+"F11.wireOp",EDGE,"E140")}),1.0]])]});
            var Q14;
            Q14=makeQuery(id+"F11.imprint","IMPRINT",FACE,{"disambiguationData":[TD([[makeQuery(id+"F11.imprint","IMPRINT",EDGE,{"derivedFrom":sQuery(id+"F11.wireOp",EDGE,"E150")}),1.0]])]});
            extrude(context, id + "F12", {"entities" : qUnion([Q0, Q1, Q2, Q3, Q4, Q5, Q6, Q7, Q8, Q9, Q10, Q11, Q12, Q13, Q14]), "operationType" : NewBodyOperationType.REMOVE, "oppositeDirection" : true, "depth" : 10 * mm});
        }
        {
            var Q0;
            Q0=makeQuery(id+"F11.imprint","IMPRINT",FACE,{"disambiguationData":[TD([[makeQuery(id+"F11.imprint","IMPRINT",EDGE,{"derivedFrom":sQuery(id+"F11.wireOp",EDGE,"E150")}),-1.0]])]});
            var Q1;
            Q1=makeQuery(id+"F11.imprint","IMPRINT",FACE,{"disambiguationData":[TD([[makeQuery(id+"F11.imprint","IMPRINT",EDGE,{"derivedFrom":sQuery(id+"F11.wireOp",EDGE,"E140")}),-1.0]])]});
            var Q2;
            Q2=makeQuery(id+"F11.imprint","IMPRINT",FACE,{"disambiguationData":[TD([[makeQuery(id+"F11.imprint","IMPRINT",EDGE,{"derivedFrom":sQuery(id+"F11.wireOp",EDGE,"E141")}),-1.0]])]});
            var Q3;
            Q3=makeQuery(id+"F11.imprint","IMPRINT",FACE,{"disambiguationData":[TD([[makeQuery(id+"F11.imprint","IMPRINT",EDGE,{"derivedFrom":sQuery(id+"F11.wireOp",EDGE,"E142")}),-1.0]])]});
            var Q4;
            Q4=makeQuery(id+"F11.imprint","IMPRINT",FACE,{"disambiguationData":[TD([[makeQuery(id+"F11.imprint","IMPRINT",EDGE,{"derivedFrom":sQuery(id+"F11.wireOp",EDGE,"E143")}),-1.0]])]});
            var Q5;
            Q5=makeQuery(id+"F11.imprint","IMPRINT",FACE,{"disambiguationData":[TD([[makeQuery(id+"F11.imprint","IMPRINT",EDGE,{"derivedFrom":sQuery(id+"F11.wireOp",EDGE,"E144")}),-1.0]])]});
            var Q6;
            Q6=makeQuery(id+"F11.imprint","IMPRINT",FACE,{"disambiguationData":[TD([[makeQuery(id+"F11.imprint","IMPRINT",EDGE,{"derivedFrom":sQuery(id+"F11.wireOp",EDGE,"E145")}),-1.0]])]});
            var Q7;
            Q7=makeQuery(id+"F11.imprint","IMPRINT",FACE,{"disambiguationData":[TD([[makeQuery(id+"F11.imprint","IMPRINT",EDGE,{"derivedFrom":sQuery(id+"F11.wireOp",EDGE,"E146")}),-1.0]])]});
            var Q8;
            Q8=makeQuery(id+"F11.imprint","IMPRINT",FACE,{"disambiguationData":[TD([[makeQuery(id+"F11.imprint","IMPRINT",EDGE,{"derivedFrom":sQuery(id+"F11.wireOp",EDGE,"E154")}),-1.0]])]});
            var Q9;
            Q9=makeQuery(id+"F11.imprint","IMPRINT",FACE,{"disambiguationData":[TD([[makeQuery(id+"F11.imprint","IMPRINT",EDGE,{"derivedFrom":sQuery(id+"F11.wireOp",EDGE,"E151")}),-1.0]])]});
            var Q10;
            Q10=makeQuery(id+"F11.imprint","IMPRINT",FACE,{"disambiguationData":[TD([[makeQuery(id+"F11.imprint","IMPRINT",EDGE,{"derivedFrom":sQuery(id+"F11.wireOp",EDGE,"E149")}),-1.0]])]});
            var Q11;
            Q11=makeQuery(id+"F11.imprint","IMPRINT",FACE,{"disambiguationData":[TD([[makeQuery(id+"F11.imprint","IMPRINT",EDGE,{"derivedFrom":sQuery(id+"F11.wireOp",EDGE,"E148")}),-1.0]])]});
            var Q12;
            Q12=makeQuery(id+"F11.imprint","IMPRINT",FACE,{"disambiguationData":[TD([[makeQuery(id+"F11.imprint","IMPRINT",EDGE,{"derivedFrom":sQuery(id+"F11.wireOp",EDGE,"E153")}),-1.0]])]});
            var Q13;
            Q13=makeQuery(id+"F11.imprint","IMPRINT",FACE,{"disambiguationData":[TD([[makeQuery(id+"F11.imprint","IMPRINT",EDGE,{"derivedFrom":sQuery(id+"F11.wireOp",EDGE,"E152")}),-1.0]])]});
            var Q14;
            Q14=makeQuery(id+"F11.imprint","IMPRINT",FACE,{"disambiguationData":[TD([[makeQuery(id+"F11.imprint","IMPRINT",EDGE,{"derivedFrom":sQuery(id+"F11.wireOp",EDGE,"E147")}),-1.0]])]});
            extrude(context, id + "F13", {"entities" : qUnion([Q0, Q1, Q2, Q3, Q4, Q5, Q6, Q7, Q8, Q9, Q10, Q11, Q12, Q13, Q14]), "operationType" : NewBodyOperationType.REMOVE, "oppositeDirection" : true, "depth" : 5.3 * mm});
        }
        {
            var Q0;
            Q0=makeQuery(id+"F2.opExtrude","SWEPT_FACE",FACE,{"disambiguationData":[OSD([sQuery(id+"F0.wireOp",EDGE,"E1.right")])]});
            var sketch = newSketch(context, id + "F14", { "sketchPlane" : qUnion([Q0])});
            skCircle(sketch, "E170", {"center": v(272.58, 5) * mm, "radius": 2.1 * mm});
            skCircle(sketch, "E171", {"center": v(237.58, 5) * mm, "radius": 2.1 * mm});
            skCircle(sketch, "E172", {"center": v(295.08, 5) * mm, "radius": 2.1 * mm});
            skCircle(sketch, "E173", {"center": v(317.58, 5) * mm, "radius": 2.1 * mm});
            skCircle(sketch, "E174", {"center": v(340.08, 5) * mm, "radius": 2.1 * mm});
            skCircle(sketch, "E175", {"center": v(362.58, 5) * mm, "radius": 2.1 * mm});
            skSolve(sketch);
        }
        {
            var Q0;
            Q0=makeQuery(id+"F14.imprint","IMPRINT",FACE,{"disambiguationData":[TD([[makeQuery(id+"F14.imprint","IMPRINT",EDGE,{"derivedFrom":sQuery(id+"F14.wireOp",EDGE,"E171")}),1.0]])]});
            var Q1;
            Q1=makeQuery(id+"F14.imprint","IMPRINT",FACE,{"disambiguationData":[TD([[makeQuery(id+"F14.imprint","IMPRINT",EDGE,{"derivedFrom":sQuery(id+"F14.wireOp",EDGE,"E170")}),1.0]])]});
            var Q2;
            Q2=makeQuery(id+"F14.imprint","IMPRINT",FACE,{"disambiguationData":[TD([[makeQuery(id+"F14.imprint","IMPRINT",EDGE,{"derivedFrom":sQuery(id+"F14.wireOp",EDGE,"E172")}),1.0]])]});
            var Q3;
            Q3=makeQuery(id+"F14.imprint","IMPRINT",FACE,{"disambiguationData":[TD([[makeQuery(id+"F14.imprint","IMPRINT",EDGE,{"derivedFrom":sQuery(id+"F14.wireOp",EDGE,"E173")}),1.0]])]});
            var Q4;
            Q4=makeQuery(id+"F14.imprint","IMPRINT",FACE,{"disambiguationData":[TD([[makeQuery(id+"F14.imprint","IMPRINT",EDGE,{"derivedFrom":sQuery(id+"F14.wireOp",EDGE,"E174")}),1.0]])]});
            var Q5;
            Q5=makeQuery(id+"F14.imprint","IMPRINT",FACE,{"disambiguationData":[TD([[makeQuery(id+"F14.imprint","IMPRINT",EDGE,{"derivedFrom":sQuery(id+"F14.wireOp",EDGE,"E175")}),1.0]])]});
            extrude(context, id + "F15", {"entities" : qUnion([Q0, Q1, Q2, Q3, Q4, Q5]), "operationType" : NewBodyOperationType.REMOVE, "oppositeDirection" : true, "depth" : 15 * mm});
        }
        {
            var Q0;
            Q0=makeQuery(id+"F2.opExtrude","SWEPT_FACE",FACE,{"disambiguationData":[OSD([sQuery(id+"F0.wireOp",EDGE,"E1.left")])]});
            var sketch = newSketch(context, id + "F16", { "sketchPlane" : qUnion([Q0])});
            skCircle(sketch, "E176", {"center": v(-295.08, 5) * mm, "radius": 2.1 * mm});
            skCircle(sketch, "E177", {"center": v(-272.58, 5) * mm, "radius": 2.1 * mm});
            skCircle(sketch, "E178", {"center": v(-237.58, 5) * mm, "radius": 2.1 * mm});
            skCircle(sketch, "E179", {"center": v(-340.08, 5) * mm, "radius": 2.1 * mm});
            skCircle(sketch, "E180", {"center": v(-362.58, 5) * mm, "radius": 2.1 * mm});
            skCircle(sketch, "E181", {"center": v(-317.58, 5) * mm, "radius": 2.1 * mm});
            skSolve(sketch);
        }
        {
            var Q0;
            Q0=makeQuery(id+"F16.imprint","IMPRINT",FACE,{"disambiguationData":[TD([[makeQuery(id+"F16.imprint","IMPRINT",EDGE,{"derivedFrom":sQuery(id+"F16.wireOp",EDGE,"E178")}),1.0]])]});
            var Q1;
            Q1=makeQuery(id+"F16.imprint","IMPRINT",FACE,{"disambiguationData":[TD([[makeQuery(id+"F16.imprint","IMPRINT",EDGE,{"derivedFrom":sQuery(id+"F16.wireOp",EDGE,"E177")}),1.0]])]});
            var Q2;
            Q2=makeQuery(id+"F16.imprint","IMPRINT",FACE,{"disambiguationData":[TD([[makeQuery(id+"F16.imprint","IMPRINT",EDGE,{"derivedFrom":sQuery(id+"F16.wireOp",EDGE,"E176")}),1.0]])]});
            var Q3;
            Q3=makeQuery(id+"F16.imprint","IMPRINT",FACE,{"disambiguationData":[TD([[makeQuery(id+"F16.imprint","IMPRINT",EDGE,{"derivedFrom":sQuery(id+"F16.wireOp",EDGE,"E181")}),1.0]])]});
            var Q4;
            Q4=makeQuery(id+"F16.imprint","IMPRINT",FACE,{"disambiguationData":[TD([[makeQuery(id+"F16.imprint","IMPRINT",EDGE,{"derivedFrom":sQuery(id+"F16.wireOp",EDGE,"E179")}),1.0]])]});
            var Q5;
            Q5=makeQuery(id+"F16.imprint","IMPRINT",FACE,{"disambiguationData":[TD([[makeQuery(id+"F16.imprint","IMPRINT",EDGE,{"derivedFrom":sQuery(id+"F16.wireOp",EDGE,"E180")}),1.0]])]});
            extrude(context, id + "F17", {"entities" : qUnion([Q0, Q1, Q2, Q3, Q4, Q5]), "operationType" : NewBodyOperationType.REMOVE, "oppositeDirection" : true, "depth" : 15 * mm});
        }
        {
            var Q0;
            Q0=makeQuery(id+"F0.imprint","IMPRINT",FACE,{"disambiguationData":[TD([[makeQuery(id+"F0.imprint","IMPRINT",EDGE,{"derivedFrom":sQuery(id+"F0.wireOp",EDGE,"E2.bottom")}),-1.0]])]});
            extrude(context, id + "F18", {"entities" : qUnion([Q0]), "depth" : 10 * mm});
        }
        {
            var Q0;
            Q0=makeQuery(id+"F0.imprint","IMPRINT",FACE,{"disambiguationData":[TD([[makeQuery(id+"F0.imprint","IMPRINT",EDGE,{"derivedFrom":sQuery(id+"F0.wireOp",EDGE,"E20.top")}),1.0]])]});
            extrude(context, id + "F19", {"entities" : qUnion([Q0]), "depth" : 10 * mm});
        }
        {
            var Q0;
            Q0=makeQuery(id+"F0.imprint","IMPRINT",FACE,{"disambiguationData":[TD([[makeQuery(id+"F0.imprint","IMPRINT",EDGE,{"derivedFrom":sQuery(id+"F0.wireOp",EDGE,"E68.bottom")}),-1.0]])]});
            extrude(context, id + "F20", {"entities" : qUnion([Q0]), "depth" : 15 * mm});
        }
        {
            var Q0;
            Q0=makeQuery(id+"F0.imprint","IMPRINT",FACE,{"disambiguationData":[TD([[makeQuery(id+"F0.imprint","IMPRINT",EDGE,{"derivedFrom":sQuery(id+"F0.wireOp",EDGE,"E92")}),-1.0]])]});
            var Q1;
            Q1=makeQuery(id+"F0.imprint","IMPRINT",FACE,{"disambiguationData":[TD([[makeQuery(id+"F0.imprint","IMPRINT",EDGE,{"derivedFrom":sQuery(id+"F0.wireOp",EDGE,"E93")}),-1.0]])]});
            var Q2;
            Q2=makeQuery(id+"F0.imprint","IMPRINT",FACE,{"disambiguationData":[TD([[makeQuery(id+"F0.imprint","IMPRINT",EDGE,{"derivedFrom":sQuery(id+"F0.wireOp",EDGE,"E94")}),-1.0]])]});
            var Q3;
            Q3=makeQuery(id+"F0.imprint","IMPRINT",FACE,{"disambiguationData":[TD([[makeQuery(id+"F0.imprint","IMPRINT",EDGE,{"derivedFrom":sQuery(id+"F0.wireOp",EDGE,"E95")}),-1.0]])]});
            extrude(context, id + "F21", {"entities" : qUnion([Q0, Q1, Q2, Q3]), "operationType" : NewBodyOperationType.ADD, "depth" : 9 * mm});
        }
        {
            var Q0;
            Q0=makeQuery(id+"F1.opExtrude","CAP_FACE",FACE,{"disambiguationData":[OSD([sQuery(id+"F0.wireOp",EDGE,"E0.bottom"),sQuery(id+"F0.wireOp",EDGE,"E0.top"),sQuery(id+"F0.wireOp",EDGE,"E0.left"),sQuery(id+"F0.wireOp",EDGE,"E0.right"),sQuery(id+"F0.wireOp",EDGE,"E38"),sQuery(id+"F0.wireOp",EDGE,"E39"),sQuery(id+"F0.wireOp",EDGE,"E40"),sQuery(id+"F0.wireOp",EDGE,"E41"),sQuery(id+"F0.wireOp",EDGE,"E42"),sQuery(id+"F0.wireOp",EDGE,"E43"),sQuery(id+"F0.wireOp",EDGE,"E44"),sQuery(id+"F0.wireOp",EDGE,"E45"),sQuery(id+"F0.wireOp",EDGE,"E46"),sQuery(id+"F0.wireOp",EDGE,"E47"),sQuery(id+"F0.wireOp",EDGE,"E48"),sQuery(id+"F0.wireOp",EDGE,"E49"),sQuery(id+"F0.wireOp",EDGE,"E50"),sQuery(id+"F0.wireOp",EDGE,"E51"),sQuery(id+"F0.wireOp",EDGE,"E52"),sQuery(id+"F0.wireOp",EDGE,"E53"),sQuery(id+"F0.wireOp",EDGE,"E54"),sQuery(id+"F0.wireOp",EDGE,"E55"),sQuery(id+"F0.wireOp",EDGE,"E56"),sQuery(id+"F0.wireOp",EDGE,"E57"),sQuery(id+"F0.wireOp",EDGE,"E58"),sQuery(id+"F0.wireOp",EDGE,"E59"),sQuery(id+"F0.wireOp",EDGE,"E60"),sQuery(id+"F0.wireOp",EDGE,"E61"),sQuery(id+"F0.wireOp",EDGE,"E63"),sQuery(id+"F0.wireOp",EDGE,"E64"),sQuery(id+"F0.wireOp",EDGE,"E65"),sQuery(id+"F0.wireOp",EDGE,"E66")])],"isStart":false});
            var sketch = newSketch(context, id + "F22", { "sketchPlane" : qUnion([Q0])});
            skLineSegment(sketch, "E182.bottom", {"start": v(-312.38, 0) * mm, "end": v(315.62, 0) * mm});
            skLineSegment(sketch, "E182.top", {"start": v(-312.38, -64) * mm, "end": v(315.62, -64) * mm});
            skArc(sketch, "E183.filletArc", {"start": v(318.62, -3) * mm, "mid": v(317.75, -0.88) * mm, "end": v(315.62, 0) * mm});
            skLineSegment(sketch, "E182.right", {"start": v(318.62, -3) * mm, "end": v(318.62, -61) * mm});
            skArc(sketch, "E184.filletArc", {"start": v(315.62, -64) * mm, "mid": v(317.75, -63.12) * mm, "end": v(318.62, -61) * mm});
            skArc(sketch, "E185.filletArc", {"start": v(-312.38, 0) * mm, "mid": v(-314.5, -0.88) * mm, "end": v(-315.38, -3) * mm});
            skLineSegment(sketch, "E182.left", {"start": v(-315.38, -3) * mm, "end": v(-315.38, -61) * mm});
            skArc(sketch, "E186.filletArc", {"start": v(-315.38, -61) * mm, "mid": v(-314.5, -63.12) * mm, "end": v(-312.38, -64) * mm});
            skSolve(sketch);
        }
        {
            var Q0;
            Q0=makeQuery(id+"F22.imprint","IMPRINT",FACE,{"disambiguationData":[TD([[makeQuery(id+"F22.imprint","IMPRINT",EDGE,{"derivedFrom":sQuery(id+"F22.wireOp",EDGE,"E182.bottom")}),-1.0]])]});
            extrude(context, id + "F23", {"entities" : qUnion([Q0]), "operationType" : NewBodyOperationType.REMOVE, "oppositeDirection" : true, "depth" : 5 * mm});
        }
    });
